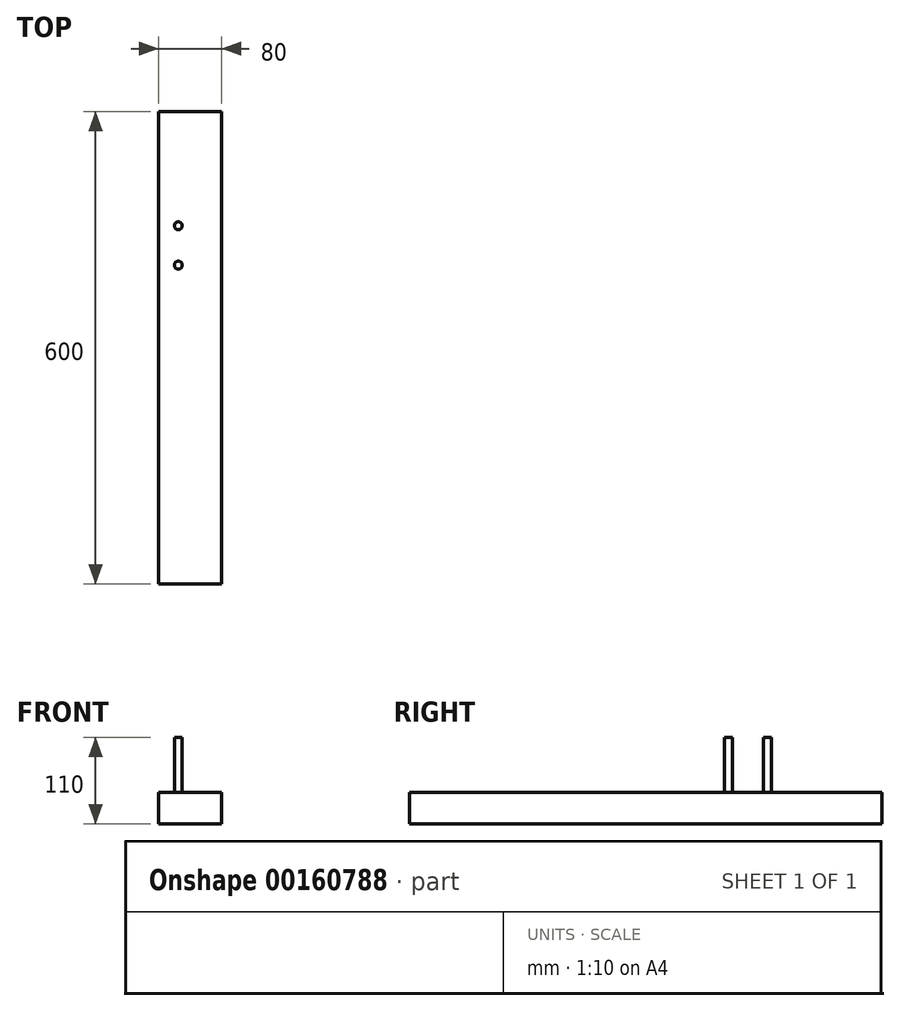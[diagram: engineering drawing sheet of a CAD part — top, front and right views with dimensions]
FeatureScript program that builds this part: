
annotation { "Feature Type Name" : "Feature", "Feature Type Description" : "" }
export const myFeature = defineFeature(function(context is Context, id is Id, definition is map)
    precondition{}
    {
        {
            var Q0;
            Q0=qCreatedBy(makeId("Top.planeOp"),FACE);
            var sketch = newSketch(context, id + "F0", { "sketchPlane" : qUnion([Q0])});
            skLineSegment(sketch, "E0.bottom", {"start": v(-40, 300) * mm, "end": v(40, 300) * mm});
            skLineSegment(sketch, "E0.top", {"start": v(-40, -300) * mm, "end": v(40, -300) * mm});
            skLineSegment(sketch, "E0.left", {"start": v(-40, 300) * mm, "end": v(-40, -300) * mm});
            skLineSegment(sketch, "E0.right", {"start": v(40, 300) * mm, "end": v(40, -300) * mm});
            skCircle(sketch, "E1", {"center": v(-15, 155) * mm, "radius": 5 * mm});
            skCircle(sketch, "E2", {"center": v(-15, 105) * mm, "radius": 5 * mm});
            skSolve(sketch);
        }
        {
            var Q0;
            Q0=makeQuery(id+"F0.imprint","IMPRINT",FACE,{"disambiguationData":[TD([[makeQuery(id+"F0.imprint","IMPRINT",EDGE,{"derivedFrom":sQuery(id+"F0.wireOp",EDGE,"E0.bottom")}),-1.0]])]});
            var Q1;
            Q1=makeQuery(id+"F0.imprint","IMPRINT",FACE,{"disambiguationData":[TD([[makeQuery(id+"F0.imprint","IMPRINT",EDGE,{"derivedFrom":sQuery(id+"F0.wireOp",EDGE,"E1")}),1.0]])]});
            var Q2;
            Q2=makeQuery(id+"F0.imprint","IMPRINT",FACE,{"disambiguationData":[TD([[makeQuery(id+"F0.imprint","IMPRINT",EDGE,{"derivedFrom":sQuery(id+"F0.wireOp",EDGE,"E2")}),1.0]])]});
            extrude(context, id + "F1", {"entities" : qUnion([Q0, Q1, Q2]), "oppositeDirection" : true, "depth" : 40 * mm});
        }
        {
            var Q0;
            Q0=makeQuery(id+"F0.imprint","IMPRINT",FACE,{"disambiguationData":[TD([[makeQuery(id+"F0.imprint","IMPRINT",EDGE,{"derivedFrom":sQuery(id+"F0.wireOp",EDGE,"E1")}),1.0]])]});
            var Q1;
            Q1=makeQuery(id+"F0.imprint","IMPRINT",FACE,{"disambiguationData":[TD([[makeQuery(id+"F0.imprint","IMPRINT",EDGE,{"derivedFrom":sQuery(id+"F0.wireOp",EDGE,"E2")}),1.0]])]});
            extrude(context, id + "F2", {"entities" : qUnion([Q0, Q1]), "operationType" : NewBodyOperationType.ADD, "depth" : 70 * mm});
        }
    });
